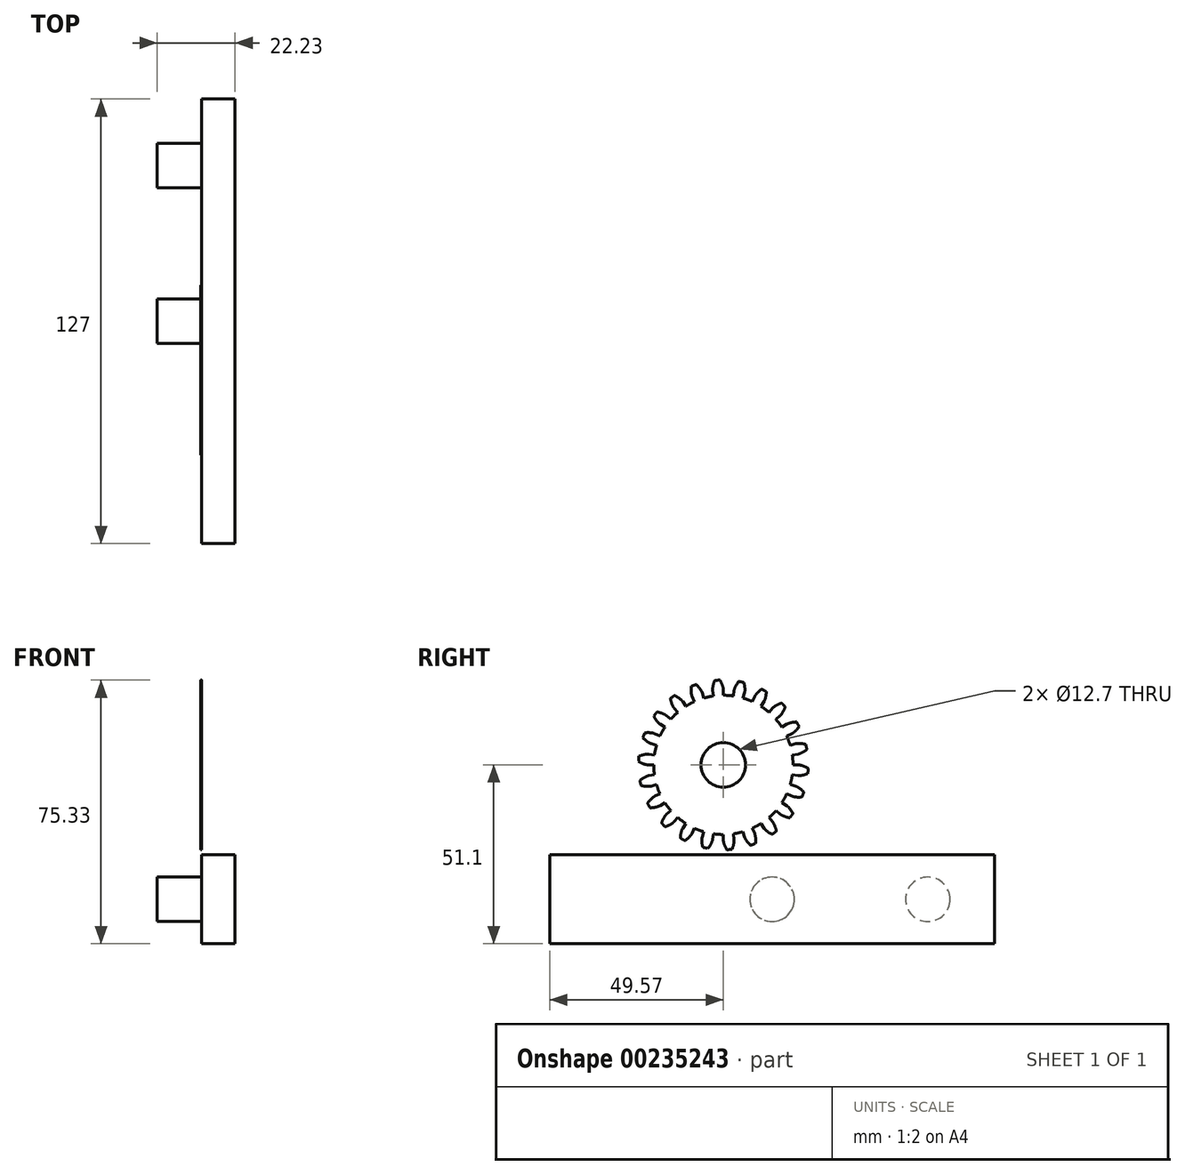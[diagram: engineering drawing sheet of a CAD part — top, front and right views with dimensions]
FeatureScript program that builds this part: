
annotation { "Feature Type Name" : "Feature", "Feature Type Description" : "" }
export const myFeature = defineFeature(function(context is Context, id is Id, definition is map)
    precondition{}
    {
        {
            assignVariable(context, id + "F0", {"name" : "NumberTeeth", "anyValue" : 22});
        }
        {
            assignVariable(context, id + "F1", {"name" : "GearThickness", "anyValue" : 0.25});
        }
        {
            var Q0;
            Q0=qCreatedBy(makeId("Right.planeOp"),FACE);
            var sketch = newSketch(context, id + "F2", { "sketchPlane" : qUnion([Q0])});
            skCircle(sketch, "E0", {"center": v(0, 0) * mm, "radius": 19.89 * mm});
            skCircle(sketch, "E1", {"center": v(0, 0) * mm, "radius": 21.52 * mm, "construction": true});
            skCircle(sketch, "E2", {"center": v(0, 0) * mm, "radius": 22.22 * mm, "construction": true});
            skCircle(sketch, "E3", {"center": v(0, 0) * mm, "radius": 24.25 * mm});
            skLineSegment(sketch, "E4", {"start": v(0, 0) * mm, "end": v(-21.52, 0) * mm, "construction": true});
            skLineSegment(sketch, "E5.1.0", {"start": v(0, 0) * mm, "end": v(-21.5, 1.08) * mm, "construction": true});
            skLineSegment(sketch, "E5.2.0", {"start": v(0, 0) * mm, "end": v(-21.4, 2.15) * mm, "construction": true});
            skLineSegment(sketch, "E5.3.0", {"start": v(0, 0) * mm, "end": v(-21.28, 3.22) * mm, "construction": true});
            skLineSegment(sketch, "E5.4.0", {"start": v(0, 0) * mm, "end": v(-21.09, 4.27) * mm, "construction": true});
            skLineSegment(sketch, "E5.5.0", {"start": v(0, 0) * mm, "end": v(-20.85, 5.32) * mm, "construction": true});
            skLineSegment(sketch, "E5.6.0", {"start": v(0, 0) * mm, "end": v(-20.56, 6.36) * mm, "construction": true});
            skLineSegment(sketch, "E5.7.0", {"start": v(0, 0) * mm, "end": v(-20.21, 7.38) * mm, "construction": true});
            skLineSegment(sketch, "E5.8.0", {"start": v(0, 0) * mm, "end": v(-19.82, 8.38) * mm, "construction": true});
            skLineSegment(sketch, "E5.9.0", {"start": v(0, 0) * mm, "end": v(-19.37, 9.36) * mm, "construction": true});
            skLineSegment(sketch, "E5.10.0", {"start": v(0, 0) * mm, "end": v(-18.88, 10.32) * mm, "construction": true});
            skLineSegment(sketch, "E5.11.0", {"start": v(0, 0) * mm, "end": v(-18.34, 11.25) * mm, "construction": true});
            skLineSegment(sketch, "E5.12.0", {"start": v(0, 0) * mm, "end": v(-17.76, 12.15) * mm, "construction": true});
            skLineSegment(sketch, "E5.13.0", {"start": v(0, 0) * mm, "end": v(-17.13, 13.02) * mm, "construction": true});
            skLineSegment(sketch, "E5.14.0", {"start": v(0, 0) * mm, "end": v(-16.46, 13.86) * mm, "construction": true});
            skLineSegment(sketch, "E5.anchor2", {"start": v(0, 0) * mm, "end": v(-16.46, 13.86) * mm, "construction": true});
            skLineSegment(sketch, "E6", {"start": v(-21.5, 1.08) * mm, "end": v(-21.54, 0) * mm, "construction": true});
            skLineSegment(sketch, "E7", {"start": v(-21.4, 2.15) * mm, "end": v(-21.62, 0) * mm, "construction": true});
            skLineSegment(sketch, "E8", {"start": v(-21.28, 3.22) * mm, "end": v(-21.76, 0.02) * mm, "construction": true});
            skLineSegment(sketch, "E9", {"start": v(-20.85, 5.32) * mm, "end": v(-22.18, 0.11) * mm, "construction": true});
            skLineSegment(sketch, "E10", {"start": v(-20.56, 6.36) * mm, "end": v(-22.46, 0.2) * mm, "construction": true});
            skLineSegment(sketch, "E11", {"start": v(-20.21, 7.38) * mm, "end": v(-22.8, 0.3) * mm, "construction": true});
            skLineSegment(sketch, "E12", {"start": v(-19.82, 8.38) * mm, "end": v(-23.17, 0.45) * mm, "construction": true});
            skLineSegment(sketch, "E13", {"start": v(-19.37, 9.36) * mm, "end": v(-23.59, 0.64) * mm, "construction": true});
            skLineSegment(sketch, "E14", {"start": v(-18.88, 10.32) * mm, "end": v(-24.04, 0.87) * mm, "construction": true});
            skLineSegment(sketch, "E15", {"start": v(-18.34, 11.25) * mm, "end": v(-24.53, 1.16) * mm, "construction": true});
            skLineSegment(sketch, "E16", {"start": v(-21.09, 4.27) * mm, "end": v(-21.94, 0.06) * mm, "construction": true});
            skLineSegment(sketch, "E17", {"start": v(-17.76, 12.15) * mm, "end": v(-25.05, 1.5) * mm, "construction": true});
            skLineSegment(sketch, "E18", {"start": v(-17.13, 13.02) * mm, "end": v(-25.6, 1.89) * mm, "construction": true});
            skLineSegment(sketch, "E19", {"start": v(-16.46, 13.86) * mm, "end": v(-26.16, 2.34) * mm, "construction": true});
            skLineSegment(sketch, "E20", {"start": v(0, 0) * mm, "end": v(-21.46, 1.54) * mm, "construction": true});
            skLineSegment(sketch, "E21", {"start": v(-19.89, 0) * mm, "end": v(-21.52, 0) * mm});
            skLineSegment(sketch, "E22.MirrorCS", {"start": v(-19.68, 2.83) * mm, "end": v(-21.3, 3.06) * mm});
            skFitSpline(sketch, "E23", {"points": [v(-21.52, 0) * mm, v(-21.54, 0) * mm, v(-21.62, 0) * mm, v(-21.76, 0.02) * mm, v(-21.94, 0.06) * mm, v(-22.18, 0.11) * mm, v(-22.46, 0.2) * mm, v(-22.8, 0.3) * mm, v(-23.17, 0.45) * mm, v(-23.59, 0.64) * mm, v(-24.04, 0.87) * mm, v(-24.53, 1.16) * mm, v(-25.05, 1.5) * mm, v(-25.6, 1.89) * mm, v(-26.16, 2.34) * mm], "startDerivative": vector(-0.77, 0) * mm, "endDerivative": vector(-1.36, 1.15) * mm});
            skLineSegment(sketch, "E24", {"start": v(-21.81, -1.32) * mm, "end": v(-26.16, 2.34) * mm, "construction": true});
            skFitSpline(sketch, "E25.MirrorCS", {"points": [v(-21.3, 3.06) * mm, v(-21.32, 3.07) * mm, v(-21.4, 3.07) * mm, v(-21.54, 3.07) * mm, v(-21.73, 3.07) * mm, v(-21.97, 3.05) * mm, v(-22.26, 3) * mm, v(-22.6, 2.94) * mm, v(-23, 2.85) * mm, v(-23.44, 2.72) * mm, v(-23.92, 2.56) * mm, v(-24.44, 2.35) * mm, v(-25, 2.09) * mm, v(-25.6, 1.77) * mm, v(-26.23, 1.4) * mm], "startDerivative": vector(-0.77, 0.11) * mm, "endDerivative": vector(-1.51, -0.94) * mm});
            skSolve(sketch);
        }
        {
            var Q0;
            {var subQ0=sQuery(id+"F2.wireOp",EDGE,"E0");var subQ27=makeQuery(id+"F2.imprint","INTERSECT",VERTEX,{"derivedFrom":[subQ0,sQuery(id+"F2.wireOp",EDGE,"10ea1024-8cf5-41f5-a75f-a634b86921f3.10.0")]});Q0=makeQuery(id+"F2.imprint","IMPRINT",FACE,{"disambiguationData":[TD([[makeQuery(id+"F2.imprint","IMPRINT",EDGE,{"disambiguationData":[TD([[subQ27,-1.0]])],"derivedFrom":subQ0}),1.0]])]});}
            var Q1;
            {var subQ0=sQuery(id+"F2.wireOp",EDGE,"10ea1024-8cf5-41f5-a75f-a634b86921f3.1.0");Q1=makeQuery(id+"F2.imprint","IMPRINT",FACE,{"disambiguationData":[TD([[makeQuery(id+"F2.imprint","IMPRINT",EDGE,{"derivedFrom":subQ0}),-1.0]])]});}
            var Q2;
            {var subQ7=sQuery(id+"F2.wireOp",EDGE,"10ea1024-8cf5-41f5-a75f-a634b86921f3.2.0");Q2=makeQuery(id+"F2.imprint","IMPRINT",FACE,{"disambiguationData":[TD([[makeQuery(id+"F2.imprint","IMPRINT",EDGE,{"derivedFrom":subQ7}),-1.0]])]});}
            var Q3;
            {var subQ8=sQuery(id+"F2.wireOp",EDGE,"10ea1024-8cf5-41f5-a75f-a634b86921f3.3.0");Q3=makeQuery(id+"F2.imprint","IMPRINT",FACE,{"disambiguationData":[TD([[makeQuery(id+"F2.imprint","IMPRINT",EDGE,{"derivedFrom":subQ8}),-1.0]])]});}
            var Q4;
            {var subQ2=sQuery(id+"F2.wireOp",EDGE,"10ea1024-8cf5-41f5-a75f-a634b86921f3.4.0");Q4=makeQuery(id+"F2.imprint","IMPRINT",FACE,{"disambiguationData":[TD([[makeQuery(id+"F2.imprint","IMPRINT",EDGE,{"derivedFrom":subQ2}),-1.0]])]});}
            var Q5;
            {var subQ8=sQuery(id+"F2.wireOp",EDGE,"10ea1024-8cf5-41f5-a75f-a634b86921f3.5.0");Q5=makeQuery(id+"F2.imprint","IMPRINT",FACE,{"disambiguationData":[TD([[makeQuery(id+"F2.imprint","IMPRINT",EDGE,{"derivedFrom":subQ8}),-1.0]])]});}
            var Q6;
            {var subQ3=sQuery(id+"F2.wireOp",EDGE,"10ea1024-8cf5-41f5-a75f-a634b86921f3.6.0");Q6=makeQuery(id+"F2.imprint","IMPRINT",FACE,{"disambiguationData":[TD([[makeQuery(id+"F2.imprint","IMPRINT",EDGE,{"derivedFrom":subQ3}),-1.0]])]});}
            var Q7;
            {var subQ0=sQuery(id+"F2.wireOp",EDGE,"10ea1024-8cf5-41f5-a75f-a634b86921f3.7.0");Q7=makeQuery(id+"F2.imprint","IMPRINT",FACE,{"disambiguationData":[TD([[makeQuery(id+"F2.imprint","IMPRINT",EDGE,{"derivedFrom":subQ0}),-1.0]])]});}
            var Q8;
            {var subQ5=sQuery(id+"F2.wireOp",EDGE,"10ea1024-8cf5-41f5-a75f-a634b86921f3.8.0");Q8=makeQuery(id+"F2.imprint","IMPRINT",FACE,{"disambiguationData":[TD([[makeQuery(id+"F2.imprint","IMPRINT",EDGE,{"derivedFrom":subQ5}),-1.0]])]});}
            var Q9;
            {var subQ1=sQuery(id+"F2.wireOp",EDGE,"10ea1024-8cf5-41f5-a75f-a634b86921f3.9.0");Q9=makeQuery(id+"F2.imprint","IMPRINT",FACE,{"disambiguationData":[TD([[makeQuery(id+"F2.imprint","IMPRINT",EDGE,{"derivedFrom":subQ1}),-1.0]])]});}
            var Q10;
            {var subQ5=sQuery(id+"F2.wireOp",EDGE,"10ea1024-8cf5-41f5-a75f-a634b86921f3.10.0");Q10=makeQuery(id+"F2.imprint","IMPRINT",FACE,{"disambiguationData":[TD([[makeQuery(id+"F2.imprint","IMPRINT",EDGE,{"derivedFrom":subQ5}),-1.0]])]});}
            var Q11;
            {var subQ8=sQuery(id+"F2.wireOp",EDGE,"10ea1024-8cf5-41f5-a75f-a634b86921f3.11.0");Q11=makeQuery(id+"F2.imprint","IMPRINT",FACE,{"disambiguationData":[TD([[makeQuery(id+"F2.imprint","IMPRINT",EDGE,{"derivedFrom":subQ8}),-1.0]])]});}
            var Q12;
            {var subQ2=sQuery(id+"F2.wireOp",EDGE,"10ea1024-8cf5-41f5-a75f-a634b86921f3.12.0");Q12=makeQuery(id+"F2.imprint","IMPRINT",FACE,{"disambiguationData":[TD([[makeQuery(id+"F2.imprint","IMPRINT",EDGE,{"derivedFrom":subQ2}),-1.0]])]});}
            var Q13;
            {var subQ3=sQuery(id+"F2.wireOp",EDGE,"10ea1024-8cf5-41f5-a75f-a634b86921f3.13.0");Q13=makeQuery(id+"F2.imprint","IMPRINT",FACE,{"disambiguationData":[TD([[makeQuery(id+"F2.imprint","IMPRINT",EDGE,{"derivedFrom":subQ3}),-1.0]])]});}
            var Q14;
            {var subQ0=sQuery(id+"F2.wireOp",EDGE,"10ea1024-8cf5-41f5-a75f-a634b86921f3.14.0");Q14=makeQuery(id+"F2.imprint","IMPRINT",FACE,{"disambiguationData":[TD([[makeQuery(id+"F2.imprint","IMPRINT",EDGE,{"derivedFrom":subQ0}),-1.0]])]});}
            var Q15;
            {var subQ6=sQuery(id+"F2.wireOp",EDGE,"10ea1024-8cf5-41f5-a75f-a634b86921f3.15.0");Q15=makeQuery(id+"F2.imprint","IMPRINT",FACE,{"disambiguationData":[TD([[makeQuery(id+"F2.imprint","IMPRINT",EDGE,{"derivedFrom":subQ6}),-1.0]])]});}
            var Q16;
            {var subQ5=sQuery(id+"F2.wireOp",EDGE,"10ea1024-8cf5-41f5-a75f-a634b86921f3.16.0");Q16=makeQuery(id+"F2.imprint","IMPRINT",FACE,{"disambiguationData":[TD([[makeQuery(id+"F2.imprint","IMPRINT",EDGE,{"derivedFrom":subQ5}),-1.0]])]});}
            var Q17;
            {var subQ7=sQuery(id+"F2.wireOp",EDGE,"10ea1024-8cf5-41f5-a75f-a634b86921f3.17.0");Q17=makeQuery(id+"F2.imprint","IMPRINT",FACE,{"disambiguationData":[TD([[makeQuery(id+"F2.imprint","IMPRINT",EDGE,{"derivedFrom":subQ7}),-1.0]])]});}
            var Q18;
            {var subQ5=sQuery(id+"F2.wireOp",EDGE,"10ea1024-8cf5-41f5-a75f-a634b86921f3.18.0");Q18=makeQuery(id+"F2.imprint","IMPRINT",FACE,{"disambiguationData":[TD([[makeQuery(id+"F2.imprint","IMPRINT",EDGE,{"derivedFrom":subQ5}),-1.0]])]});}
            var Q19;
            {var subQ8=sQuery(id+"F2.wireOp",EDGE,"10ea1024-8cf5-41f5-a75f-a634b86921f3.19.0");Q19=makeQuery(id+"F2.imprint","IMPRINT",FACE,{"disambiguationData":[TD([[makeQuery(id+"F2.imprint","IMPRINT",EDGE,{"derivedFrom":subQ8}),-1.0]])]});}
            var Q20;
            {var subQ8=sQuery(id+"F2.wireOp",EDGE,"E21");Q20=makeQuery(id+"F2.imprint","IMPRINT",FACE,{"disambiguationData":[TD([[makeQuery(id+"F2.imprint","IMPRINT",EDGE,{"derivedFrom":subQ8}),-1.0]])]});}
            extrude(context, id + "F3", {"entities" : qUnion([Q0, Q1, Q2, Q3, Q4, Q5, Q6, Q7, Q8, Q9, Q10, Q11, Q12, Q13, Q14, Q15, Q16, Q17, Q18, Q19, Q20]), "depth" : (getVariable(context, 'GearThickness')) * mm});
        }
        {
            var Q0;
            Q0=makeQuery(id+"F3.opExtrude","SWEPT_FACE",FACE,{"disambiguationData":[OSD([sQuery(id+"F2.wireOp",EDGE,"E25.MirrorCS")])]});
            var Q1;
            Q1=makeQuery(id+"F3.opExtrude","SWEPT_FACE",FACE,{"disambiguationData":[OSD([sQuery(id+"F2.wireOp",EDGE,"E23")])]});
            var Q2;
            Q2=makeQuery(id+"F3.opExtrude","SWEPT_FACE",FACE,{"disambiguationData":[OSD([sQuery(id+"F2.wireOp",EDGE,"E3")])]});
            var Q3;
            Q3=makeQuery(id+"F3.opExtrude","SWEPT_FACE",FACE,{"disambiguationData":[OSD([sQuery(id+"F2.wireOp",EDGE,"E22.MirrorCS")])]});
            var Q4;
            Q4=makeQuery(id+"F3.opExtrude","SWEPT_FACE",FACE,{"disambiguationData":[OSD([sQuery(id+"F2.wireOp",EDGE,"E21")])]});
            var Q5;
            Q5=makeQuery(id+"F3.opExtrude","SWEPT_FACE",FACE,{"disambiguationData":[OSD([sQuery(id+"F2.wireOp",EDGE,"E0")])]});
            circularPattern(context, id + "F4", {"faces" : qUnion([Q0, Q1, Q2, Q3, Q4]), "axis" : qUnion([Q5]), "angle" : 360 * degree, "instanceCount" : getVariable(context, 'NumberTeeth'), "equalSpace" : true, "patternType" : PatternType.FACE});
        }
        {
            var Q0;
            Q0=makeQuery(id+"F3.opExtrude","CAP_FACE",FACE,{"disambiguationData":[OSD([sQuery(id+"F2.wireOp",EDGE,"E0"),sQuery(id+"F2.wireOp",EDGE,"E3"),sQuery(id+"F2.wireOp",EDGE,"E21"),sQuery(id+"F2.wireOp",EDGE,"E22.MirrorCS"),sQuery(id+"F2.wireOp",EDGE,"E23"),sQuery(id+"F2.wireOp",EDGE,"E25.MirrorCS")])],"isStart":false});
            var sketch = newSketch(context, id + "F5", { "sketchPlane" : qUnion([Q0])});
            skCircle(sketch, "E26", {"center": v(0, 0) * mm, "radius": 6.35 * mm});
            skSolve(sketch);
        }
        {
            var Q0;
            Q0 = qSketchRegion(id + "F5", true);
            extrude(context, id + "F6", {"entities" : qUnion([Q0]), "operationType" : NewBodyOperationType.REMOVE, "endBound" : BoundingType.THROUGH_ALL, "oppositeDirection" : true, "depth" : 25.4 * mm});
        }
        {
            var Q0;
            Q0=makeQuery(id+"F3.opExtrude","CAP_FACE",FACE,{"disambiguationData":[OSD([sQuery(id+"F2.wireOp",EDGE,"E0"),sQuery(id+"F2.wireOp",EDGE,"E3"),sQuery(id+"F2.wireOp",EDGE,"E21"),sQuery(id+"F2.wireOp",EDGE,"E22.MirrorCS"),sQuery(id+"F2.wireOp",EDGE,"E23"),sQuery(id+"F2.wireOp",EDGE,"E25.MirrorCS")])],"isStart":false});
            var sketch = newSketch(context, id + "F7", { "sketchPlane" : qUnion([Q0])});
            skLineSegment(sketch, "E27.bottom", {"start": v(-49.57, -25.7) * mm, "end": v(77.43, -25.7) * mm});
            skLineSegment(sketch, "E27.top", {"start": v(-49.57, -51.1) * mm, "end": v(77.43, -51.1) * mm});
            skLineSegment(sketch, "E27.left", {"start": v(-49.57, -25.7) * mm, "end": v(-49.57, -51.1) * mm});
            skLineSegment(sketch, "E27.right", {"start": v(77.43, -25.7) * mm, "end": v(77.43, -51.1) * mm});
            skSolve(sketch);
        }
        {
            var Q0;
            Q0 = qSketchRegion(id + "F7", true);
            extrude(context, id + "F8", {"entities" : qUnion([Q0]), "depth" : 9.52 * mm});
        }
        {
            var Q0;
            Q0=makeQuery(id+"F8.opExtrude","CAP_FACE",FACE,{"disambiguationData":[OSD([sQuery(id+"F7.wireOp",EDGE,"E27.bottom"),sQuery(id+"F7.wireOp",EDGE,"E27.top"),sQuery(id+"F7.wireOp",EDGE,"E27.left"),sQuery(id+"F7.wireOp",EDGE,"E27.right")])],"isStart":true});
            var sketch = newSketch(context, id + "F9", { "sketchPlane" : qUnion([Q0])});
            skCircle(sketch, "E28", {"center": v(-58.38, -38.4) * mm, "radius": 6.35 * mm});
            skSolve(sketch);
        }
        {
            var Q0;
            Q0 = qSketchRegion(id + "F9", true);
            extrude(context, id + "F10", {"entities" : qUnion([Q0]), "operationType" : NewBodyOperationType.ADD, "depth" : 12.7 * mm});
        }
        {
            var Q0;
            Q0=makeQuery(id+"F8.opExtrude","CAP_FACE",FACE,{"disambiguationData":[OSD([sQuery(id+"F7.wireOp",EDGE,"E27.bottom"),sQuery(id+"F7.wireOp",EDGE,"E27.top"),sQuery(id+"F7.wireOp",EDGE,"E27.left"),sQuery(id+"F7.wireOp",EDGE,"E27.right")])],"isStart":true});
            var sketch = newSketch(context, id + "F11", { "sketchPlane" : qUnion([Q0])});
            skCircle(sketch, "E29", {"center": v(-13.93, -38.4) * mm, "radius": 6.35 * mm});
            skSolve(sketch);
        }
        {
            var Q0;
            Q0 = qSketchRegion(id + "F11", true);
            extrude(context, id + "F12", {"entities" : qUnion([Q0]), "operationType" : NewBodyOperationType.ADD, "depth" : 12.7 * mm});
        }
        {
            var Q0;
            Q0=makeQuery(id+"F3.opExtrude","SWEPT_BODY",BODY,{"disambiguationData":[OSD([sQuery(id+"F2.wireOp",EDGE,"E0"),sQuery(id+"F2.wireOp",EDGE,"E3"),sQuery(id+"F2.wireOp",EDGE,"E21"),sQuery(id+"F2.wireOp",EDGE,"E22.MirrorCS"),sQuery(id+"F2.wireOp",EDGE,"E23"),sQuery(id+"F2.wireOp",EDGE,"E25.MirrorCS")])]});
            transform(context, id + "F13", {"entities" : qUnion([Q0]), "transformType" : TransformType.TRANSLATION_3D, "dx" : 0 * mm, "dy" : 0 * mm, "dz" : 0 * mm, "makeCopy" : true});
        }
    });
